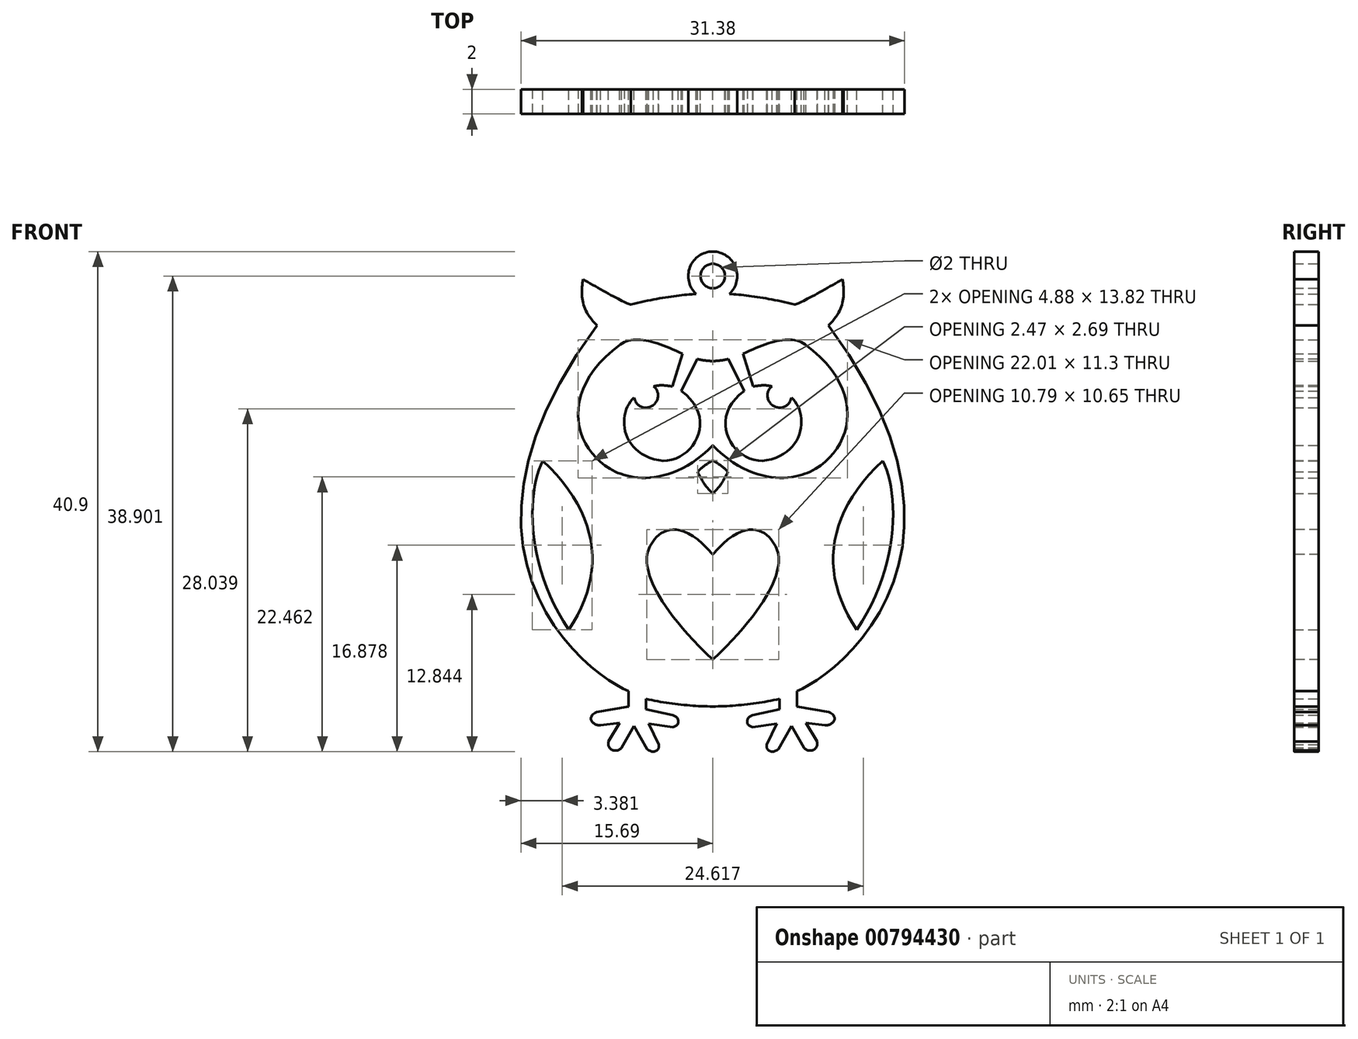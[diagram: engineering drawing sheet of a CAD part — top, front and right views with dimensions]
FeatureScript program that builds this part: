
annotation { "Feature Type Name" : "Feature", "Feature Type Description" : "" }
export const myFeature = defineFeature(function(context is Context, id is Id, definition is map)
    precondition{}
    {
        {
            var Q0;
            Q0=qCreatedBy(makeId("Front.planeOp"),FACE);
            var sketch = newSketch(context, id + "F0", { "sketchPlane" : qUnion([Q0])});
            skLineSegment(sketch, "E0", {"start": v(-16.23, -20) * mm, "end": v(16.23, 20) * mm, "construction": true});
            skFitSpline(sketch, "E1", {"points": [v(-6.7, 17.41) * mm, v(0, 18.33) * mm], "startDerivative": vector(8.77, 2.26) * mm, "endDerivative": vector(4.3, 0) * mm});
            skFitSpline(sketch, "E2", {"points": [v(-6.7, 17.41) * mm, v(-10.62, 19.48) * mm], "startDerivative": vector(-0.95, 0) * mm, "endDerivative": vector(-4.32, 2.45) * mm});
            skFitSpline(sketch, "E3", {"points": [v(-10.62, 19.48) * mm, v(-9.46, 15.72) * mm], "startDerivative": vector(-0.45, -3.6) * mm, "endDerivative": vector(4.32, -4) * mm});
            skFitSpline(sketch, "E4", {"points": [v(-9.46, 15.72) * mm, v(-6.88, -14.19) * mm], "startDerivative": vector(-42.09, -56.82) * mm, "endDerivative": vector(8.88, -3.32) * mm});
            skFitSpline(sketch, "E5", {"points": [v(-6.88, -14.19) * mm, v(-6.88, -15.47) * mm], "startDerivative": vector(0, -1.28) * mm, "endDerivative": vector(0, -1.28) * mm});
            skFitSpline(sketch, "E6", {"points": [v(-6.88, -15.47) * mm, v(-9.5, -15.9) * mm], "startDerivative": vector(-2.62, -0.44) * mm, "endDerivative": vector(-2.62, -0.44) * mm});
            skFitSpline(sketch, "E7", {"points": [v(-9.5, -15.9) * mm, v(-9.18, -16.99) * mm], "startDerivative": vector(-2.96, -1.5) * mm, "endDerivative": vector(1.5, 0.32) * mm});
            skFitSpline(sketch, "E8", {"points": [v(-9.18, -16.99) * mm, v(-7.63, -16.8) * mm], "startDerivative": vector(1.55, 0.18) * mm, "endDerivative": vector(1.55, 0.18) * mm});
            skFitSpline(sketch, "E9", {"points": [v(-7.63, -16.8) * mm, v(-8.53, -18.34) * mm], "startDerivative": vector(-0.9, -1.53) * mm, "endDerivative": vector(-0.9, -1.53) * mm});
            skFitSpline(sketch, "E10", {"points": [v(-8.53, -18.34) * mm, v(-7.47, -18.84) * mm], "startDerivative": vector(-0.36, -2.55) * mm, "endDerivative": vector(0.87, 1.14) * mm});
            skFitSpline(sketch, "E11", {"points": [v(-7.47, -18.84) * mm, v(-6.45, -17.05) * mm], "startDerivative": vector(1.02, 1.8) * mm, "endDerivative": vector(1.02, 1.8) * mm});
            skFitSpline(sketch, "E12", {"points": [v(-6.45, -17.05) * mm, v(-5.37, -18.98) * mm], "startDerivative": vector(1.08, -1.93) * mm, "endDerivative": vector(1.08, -1.93) * mm});
            skFitSpline(sketch, "E13", {"points": [v(-5.37, -18.98) * mm, v(-4.43, -18.58) * mm], "startDerivative": vector(2.05, -1.28) * mm, "endDerivative": vector(-0.32, 1.1) * mm});
            skFitSpline(sketch, "E14", {"points": [v(-4.43, -18.58) * mm, v(-5.23, -16.88) * mm], "startDerivative": vector(-0.8, 1.7) * mm, "endDerivative": vector(-0.8, 1.7) * mm});
            skFitSpline(sketch, "E15", {"points": [v(-5.23, -16.88) * mm, v(-3.26, -17.14) * mm], "startDerivative": vector(1.97, -0.26) * mm, "endDerivative": vector(1.97, -0.26) * mm});
            skFitSpline(sketch, "E16", {"points": [v(-3.26, -17.14) * mm, v(-3.26, -16.18) * mm], "startDerivative": vector(1.96, 0.27) * mm, "endDerivative": vector(-1.6, 0.32) * mm});
            skFitSpline(sketch, "E17", {"points": [v(-3.26, -16.18) * mm, v(-5.46, -15.68) * mm], "startDerivative": vector(-2.2, 0.5) * mm, "endDerivative": vector(-2.2, 0.5) * mm});
            skFitSpline(sketch, "E18", {"points": [v(-5.46, -15.68) * mm, v(-5.46, -14.83) * mm], "startDerivative": vector(0, 0.85) * mm, "endDerivative": vector(0, 0.85) * mm});
            skFitSpline(sketch, "E19", {"points": [v(-5.46, -14.83) * mm, v(0, -15.47) * mm], "startDerivative": vector(5.42, -1.32) * mm, "endDerivative": vector(5.24, -0.12) * mm});
            skFitSpline(sketch, "E20", {"points": [v(-13.9, 4.64) * mm, v(-11.77, -9.18) * mm], "startDerivative": vector(-4.05, -7.66) * mm, "endDerivative": vector(10.64, -15.64) * mm});
            skFitSpline(sketch, "E21", {"points": [v(-13.9, 4.64) * mm, v(-11.77, -9.18) * mm], "startDerivative": vector(13.96, -13.18) * mm, "endDerivative": vector(-9.2, -13.72) * mm});
            skFitSpline(sketch, "E22", {"points": [v(0, 12.8) * mm, v(-1.27, 12.97) * mm], "startDerivative": vector(-1.5, 0.04) * mm, "endDerivative": vector(-1.22, 0.31) * mm});
            skFitSpline(sketch, "E23", {"points": [v(-1.27, 12.97) * mm, v(-2.57, 10.35) * mm], "startDerivative": vector(-1.3, -2.62) * mm, "endDerivative": vector(-1.3, -2.62) * mm});
            skFitSpline(sketch, "E24", {"points": [v(-2.57, 10.35) * mm, v(-4.8, 4.76) * mm], "startDerivative": vector(9.95, -7.21) * mm, "endDerivative": vector(-8.57, 2.6) * mm});
            skFitSpline(sketch, "E25", {"points": [v(-4.8, 4.76) * mm, v(-6.43, 9.81) * mm], "startDerivative": vector(-8.74, 2.65) * mm, "endDerivative": vector(3.84, 3.47) * mm});
            skFitSpline(sketch, "E26", {"points": [v(-6.43, 9.81) * mm, v(-4.84, 9.21) * mm], "startDerivative": vector(0.77, -3.16) * mm, "endDerivative": vector(1.08, 0.94) * mm});
            skFitSpline(sketch, "E27", {"points": [v(-4.84, 9.21) * mm, v(-4.84, 10.71) * mm], "startDerivative": vector(1.62, 1.4) * mm, "endDerivative": vector(-1.29, 0.77) * mm});
            skFitSpline(sketch, "E28", {"points": [v(-4.84, 10.71) * mm, v(-3.32, 10.71) * mm], "startDerivative": vector(1.16, 0.39) * mm, "endDerivative": vector(2, -0.39) * mm});
            skFitSpline(sketch, "E29", {"points": [v(-3.32, 10.71) * mm, v(-2.48, 13.38) * mm], "startDerivative": vector(0.84, 2.66) * mm, "endDerivative": vector(0.84, 2.66) * mm});
            skFitSpline(sketch, "E30", {"points": [v(-2.48, 13.38) * mm, v(-7.55, 14.15) * mm], "startDerivative": vector(-6.19, 3.03) * mm, "endDerivative": vector(-3.45, -2.5) * mm});
            skFitSpline(sketch, "E31", {"points": [v(-7.55, 14.15) * mm, v(-7.98, 3.75) * mm], "startDerivative": vector(-15.56, -11.26) * mm, "endDerivative": vector(10.36, -5) * mm});
            skFitSpline(sketch, "E32", {"points": [v(-7.98, 3.75) * mm, v(0, 5.9) * mm], "startDerivative": vector(4.78, -2.3) * mm, "endDerivative": vector(9.63, 9.73) * mm});
            skFitSpline(sketch, "E33", {"points": [v(0, 4.66) * mm, v(-1.23, 3.73) * mm], "startDerivative": vector(-1.31, -0.7) * mm, "endDerivative": vector(-1.03, -1.22) * mm});
            skFitSpline(sketch, "E34", {"points": [v(-1.23, 3.73) * mm, v(0, 1.97) * mm], "startDerivative": vector(0.97, -1.93) * mm, "endDerivative": vector(1.83, -1.55) * mm});
            skLineSegment(sketch, "E35", {"start": v(0, 18.33) * mm, "end": v(0, -15.47) * mm, "construction": true});
            skFitSpline(sketch, "E36.MirrorCS", {"points": [v(3.26, -17.14) * mm, v(3.26, -16.18) * mm], "startDerivative": vector(-1.96, 0.27) * mm, "endDerivative": vector(1.6, 0.32) * mm});
            skFitSpline(sketch, "E37.MirrorCS", {"points": [v(6.88, -14.19) * mm, v(6.88, -15.47) * mm], "startDerivative": vector(0, -1.28) * mm, "endDerivative": vector(0, -1.28) * mm});
            skFitSpline(sketch, "E38.MirrorCS", {"points": [v(7.63, -16.8) * mm, v(8.53, -18.34) * mm], "startDerivative": vector(0.9, -1.53) * mm, "endDerivative": vector(0.9, -1.53) * mm});
            skFitSpline(sketch, "E39.MirrorCS", {"points": [v(9.18, -16.99) * mm, v(7.63, -16.8) * mm], "startDerivative": vector(-1.55, 0.18) * mm, "endDerivative": vector(-1.55, 0.18) * mm});
            skFitSpline(sketch, "E40.MirrorCS", {"points": [v(0, 4.66) * mm, v(1.23, 3.73) * mm], "startDerivative": vector(1.31, -0.7) * mm, "endDerivative": vector(1.03, -1.22) * mm});
            skFitSpline(sketch, "E41.MirrorCS", {"points": [v(4.84, 10.71) * mm, v(3.32, 10.71) * mm], "startDerivative": vector(-1.16, 0.39) * mm, "endDerivative": vector(-2, -0.39) * mm});
            skFitSpline(sketch, "E42.MirrorCS", {"points": [v(4.84, 9.21) * mm, v(4.84, 10.71) * mm], "startDerivative": vector(-1.62, 1.4) * mm, "endDerivative": vector(1.29, 0.77) * mm});
            skFitSpline(sketch, "E43.MirrorCS", {"points": [v(5.46, -15.68) * mm, v(5.46, -14.83) * mm], "startDerivative": vector(0, 0.85) * mm, "endDerivative": vector(0, 0.85) * mm});
            skFitSpline(sketch, "E44.MirrorCS", {"points": [v(0, 12.8) * mm, v(1.27, 12.97) * mm], "startDerivative": vector(1.5, 0.04) * mm, "endDerivative": vector(1.22, 0.31) * mm});
            skFitSpline(sketch, "E45.MirrorCS", {"points": [v(5.37, -18.98) * mm, v(4.43, -18.58) * mm], "startDerivative": vector(-2.05, -1.28) * mm, "endDerivative": vector(0.32, 1.1) * mm});
            skFitSpline(sketch, "E46.MirrorCS", {"points": [v(8.53, -18.34) * mm, v(7.47, -18.84) * mm], "startDerivative": vector(0.36, -2.55) * mm, "endDerivative": vector(-0.87, 1.14) * mm});
            skFitSpline(sketch, "E47.MirrorCS", {"points": [v(7.47, -18.84) * mm, v(6.45, -17.05) * mm], "startDerivative": vector(-1.02, 1.8) * mm, "endDerivative": vector(-1.02, 1.8) * mm});
            skFitSpline(sketch, "E48.MirrorCS", {"points": [v(3.26, -16.18) * mm, v(5.46, -15.68) * mm], "startDerivative": vector(2.2, 0.5) * mm, "endDerivative": vector(2.2, 0.5) * mm});
            skFitSpline(sketch, "E49.MirrorCS", {"points": [v(6.45, -17.05) * mm, v(5.37, -18.98) * mm], "startDerivative": vector(-1.08, -1.93) * mm, "endDerivative": vector(-1.08, -1.93) * mm});
            skFitSpline(sketch, "E50.MirrorCS", {"points": [v(5.23, -16.88) * mm, v(3.26, -17.14) * mm], "startDerivative": vector(-1.97, -0.26) * mm, "endDerivative": vector(-1.97, -0.26) * mm});
            skFitSpline(sketch, "E51.MirrorCS", {"points": [v(4.43, -18.58) * mm, v(5.23, -16.88) * mm], "startDerivative": vector(0.8, 1.7) * mm, "endDerivative": vector(0.8, 1.7) * mm});
            skFitSpline(sketch, "E52.MirrorCS", {"points": [v(1.27, 12.97) * mm, v(2.57, 10.35) * mm], "startDerivative": vector(1.3, -2.62) * mm, "endDerivative": vector(1.3, -2.62) * mm});
            skFitSpline(sketch, "E53.MirrorCS", {"points": [v(6.7, 17.41) * mm, v(10.62, 19.48) * mm], "startDerivative": vector(0.95, 0) * mm, "endDerivative": vector(4.32, 2.45) * mm});
            skFitSpline(sketch, "E54.MirrorCS", {"points": [v(10.62, 19.48) * mm, v(9.46, 15.72) * mm], "startDerivative": vector(0.45, -3.6) * mm, "endDerivative": vector(-4.32, -4) * mm});
            skFitSpline(sketch, "E55.MirrorCS", {"points": [v(6.88, -15.47) * mm, v(9.5, -15.9) * mm], "startDerivative": vector(2.62, -0.44) * mm, "endDerivative": vector(2.62, -0.44) * mm});
            skFitSpline(sketch, "E56.MirrorCS", {"points": [v(9.5, -15.9) * mm, v(9.18, -16.99) * mm], "startDerivative": vector(2.96, -1.5) * mm, "endDerivative": vector(-1.5, 0.32) * mm});
            skFitSpline(sketch, "E57.MirrorCS", {"points": [v(1.23, 3.73) * mm, v(0, 1.97) * mm], "startDerivative": vector(-0.97, -1.93) * mm, "endDerivative": vector(-1.83, -1.55) * mm});
            skFitSpline(sketch, "E58.MirrorCS", {"points": [v(6.43, 9.81) * mm, v(4.84, 9.21) * mm], "startDerivative": vector(-0.77, -3.16) * mm, "endDerivative": vector(-1.08, 0.94) * mm});
            skFitSpline(sketch, "E59.MirrorCS", {"points": [v(3.32, 10.71) * mm, v(2.48, 13.38) * mm], "startDerivative": vector(-0.84, 2.66) * mm, "endDerivative": vector(-0.84, 2.66) * mm});
            skFitSpline(sketch, "E60.MirrorCS", {"points": [v(2.48, 13.38) * mm, v(7.55, 14.15) * mm], "startDerivative": vector(6.19, 3.03) * mm, "endDerivative": vector(3.45, -2.5) * mm});
            skLineSegment(sketch, "E61.MirrorCS", {"start": v(16.23, -20) * mm, "end": v(-16.23, 20) * mm, "construction": true});
            skFitSpline(sketch, "E62.MirrorCS", {"points": [v(6.7, 17.41) * mm, v(0, 18.33) * mm], "startDerivative": vector(-8.77, 2.26) * mm, "endDerivative": vector(-4.3, 0) * mm});
            skFitSpline(sketch, "E63.MirrorCS", {"points": [v(2.57, 10.35) * mm, v(4.8, 4.76) * mm], "startDerivative": vector(-9.95, -7.21) * mm, "endDerivative": vector(8.57, 2.6) * mm});
            skFitSpline(sketch, "E64.MirrorCS", {"points": [v(9.46, 15.72) * mm, v(6.88, -14.19) * mm], "startDerivative": vector(42.09, -56.82) * mm, "endDerivative": vector(-8.88, -3.32) * mm});
            skFitSpline(sketch, "E65.MirrorCS", {"points": [v(4.8, 4.76) * mm, v(6.43, 9.81) * mm], "startDerivative": vector(8.74, 2.65) * mm, "endDerivative": vector(-3.84, 3.47) * mm});
            skFitSpline(sketch, "E66.MirrorCS", {"points": [v(7.98, 3.75) * mm, v(0, 5.9) * mm], "startDerivative": vector(-4.78, -2.3) * mm, "endDerivative": vector(-9.63, 9.73) * mm});
            skFitSpline(sketch, "E67.MirrorCS", {"points": [v(5.46, -14.83) * mm, v(0, -15.47) * mm], "startDerivative": vector(-5.42, -1.32) * mm, "endDerivative": vector(-5.24, -0.12) * mm});
            skFitSpline(sketch, "E68.MirrorCS", {"points": [v(13.9, 4.64) * mm, v(11.77, -9.18) * mm], "startDerivative": vector(4.05, -7.66) * mm, "endDerivative": vector(-10.64, -15.64) * mm});
            skFitSpline(sketch, "E69.MirrorCS", {"points": [v(7.55, 14.15) * mm, v(7.98, 3.75) * mm], "startDerivative": vector(15.56, -11.26) * mm, "endDerivative": vector(-10.36, -5) * mm});
            skFitSpline(sketch, "E70.MirrorCS", {"points": [v(13.9, 4.64) * mm, v(11.77, -9.18) * mm], "startDerivative": vector(-13.96, -13.18) * mm, "endDerivative": vector(9.2, -13.72) * mm});
            skCircle(sketch, "E71", {"center": v(0, 19.75) * mm, "radius": 2 * mm});
            skCircle(sketch, "E72", {"center": v(0, 19.75) * mm, "radius": 1 * mm});
            skPoint(sketch, "E73", {"position": v(0, 20) * mm});
            skSolve(sketch);
        }
        {
            var Q0;
            Q0 = qSketchRegion(id + "F0", true);
            extrude(context, id + "F1", {"entities" : qUnion([Q0]), "depth" : 2 * mm, "offsetDistance" : 25 * mm});
        }
        {
            var Q0;
            Q0=makeQuery(id+"F1.opExtrude","CAP_FACE",FACE,{"disambiguationData":[OSD([sQuery(id+"F0.wireOp",EDGE,"E1"),sQuery(id+"F0.wireOp",EDGE,"E2"),sQuery(id+"F0.wireOp",EDGE,"E3"),sQuery(id+"F0.wireOp",EDGE,"E4"),sQuery(id+"F0.wireOp",EDGE,"E5"),sQuery(id+"F0.wireOp",EDGE,"E6"),sQuery(id+"F0.wireOp",EDGE,"E7"),sQuery(id+"F0.wireOp",EDGE,"E8"),sQuery(id+"F0.wireOp",EDGE,"E9"),sQuery(id+"F0.wireOp",EDGE,"E10"),sQuery(id+"F0.wireOp",EDGE,"E11"),sQuery(id+"F0.wireOp",EDGE,"E12"),sQuery(id+"F0.wireOp",EDGE,"E13"),sQuery(id+"F0.wireOp",EDGE,"E14"),sQuery(id+"F0.wireOp",EDGE,"E15"),sQuery(id+"F0.wireOp",EDGE,"E16"),sQuery(id+"F0.wireOp",EDGE,"E17"),sQuery(id+"F0.wireOp",EDGE,"E18"),sQuery(id+"F0.wireOp",EDGE,"E19"),sQuery(id+"F0.wireOp",EDGE,"E20"),sQuery(id+"F0.wireOp",EDGE,"E21"),sQuery(id+"F0.wireOp",EDGE,"E22"),sQuery(id+"F0.wireOp",EDGE,"E23"),sQuery(id+"F0.wireOp",EDGE,"E24"),sQuery(id+"F0.wireOp",EDGE,"E25"),sQuery(id+"F0.wireOp",EDGE,"E26"),sQuery(id+"F0.wireOp",EDGE,"E27"),sQuery(id+"F0.wireOp",EDGE,"E28"),sQuery(id+"F0.wireOp",EDGE,"E29"),sQuery(id+"F0.wireOp",EDGE,"E30"),sQuery(id+"F0.wireOp",EDGE,"E31"),sQuery(id+"F0.wireOp",EDGE,"E32"),sQuery(id+"F0.wireOp",EDGE,"E33"),sQuery(id+"F0.wireOp",EDGE,"E34"),sQuery(id+"F0.wireOp",EDGE,"E36.MirrorCS"),sQuery(id+"F0.wireOp",EDGE,"E37.MirrorCS"),sQuery(id+"F0.wireOp",EDGE,"E38.MirrorCS"),sQuery(id+"F0.wireOp",EDGE,"E39.MirrorCS"),sQuery(id+"F0.wireOp",EDGE,"E40.MirrorCS"),sQuery(id+"F0.wireOp",EDGE,"E41.MirrorCS"),sQuery(id+"F0.wireOp",EDGE,"E42.MirrorCS"),sQuery(id+"F0.wireOp",EDGE,"E43.MirrorCS"),sQuery(id+"F0.wireOp",EDGE,"E44.MirrorCS"),sQuery(id+"F0.wireOp",EDGE,"E45.MirrorCS"),sQuery(id+"F0.wireOp",EDGE,"E46.MirrorCS"),sQuery(id+"F0.wireOp",EDGE,"E47.MirrorCS"),sQuery(id+"F0.wireOp",EDGE,"E48.MirrorCS"),sQuery(id+"F0.wireOp",EDGE,"E49.MirrorCS"),sQuery(id+"F0.wireOp",EDGE,"E50.MirrorCS"),sQuery(id+"F0.wireOp",EDGE,"E51.MirrorCS"),sQuery(id+"F0.wireOp",EDGE,"E52.MirrorCS"),sQuery(id+"F0.wireOp",EDGE,"E53.MirrorCS"),sQuery(id+"F0.wireOp",EDGE,"E54.MirrorCS"),sQuery(id+"F0.wireOp",EDGE,"E55.MirrorCS"),sQuery(id+"F0.wireOp",EDGE,"E56.MirrorCS"),sQuery(id+"F0.wireOp",EDGE,"E57.MirrorCS"),sQuery(id+"F0.wireOp",EDGE,"E58.MirrorCS"),sQuery(id+"F0.wireOp",EDGE,"E59.MirrorCS"),sQuery(id+"F0.wireOp",EDGE,"E60.MirrorCS"),sQuery(id+"F0.wireOp",EDGE,"E62.MirrorCS"),sQuery(id+"F0.wireOp",EDGE,"E63.MirrorCS"),sQuery(id+"F0.wireOp",EDGE,"E64.MirrorCS"),sQuery(id+"F0.wireOp",EDGE,"E65.MirrorCS"),sQuery(id+"F0.wireOp",EDGE,"E66.MirrorCS"),sQuery(id+"F0.wireOp",EDGE,"E67.MirrorCS"),sQuery(id+"F0.wireOp",EDGE,"E68.MirrorCS"),sQuery(id+"F0.wireOp",EDGE,"E69.MirrorCS"),sQuery(id+"F0.wireOp",EDGE,"E70.MirrorCS"),sQuery(id+"F0.wireOp",EDGE,"E71"),sQuery(id+"F0.wireOp",EDGE,"E72")])],"isStart":false});
            var sketch = newSketch(context, id + "F2", { "sketchPlane" : qUnion([Q0])});
            skLineSegment(sketch, "E74", {"start": v(0, 0) * mm, "end": v(0, -15.47) * mm, "construction": true});
            skFitSpline(sketch, "E75", {"points": [v(0, -11.63) * mm, v(-5.37, -3.03) * mm], "startDerivative": vector(-13.5, 12.8) * mm, "endDerivative": vector(0.76, 4.57) * mm});
            skFitSpline(sketch, "E76", {"points": [v(-5.37, -3.03) * mm, v(0, -3.03) * mm], "startDerivative": vector(0.54, 3.25) * mm, "endDerivative": vector(10.25, -12.03) * mm});
            skFitSpline(sketch, "E77.MirrorCS", {"points": [v(5.37, -3.03) * mm, v(0, -3.03) * mm], "startDerivative": vector(-0.54, 3.25) * mm, "endDerivative": vector(-10.25, -12.03) * mm});
            skFitSpline(sketch, "E78.MirrorCS", {"points": [v(0, -11.63) * mm, v(5.37, -3.03) * mm], "startDerivative": vector(13.5, 12.8) * mm, "endDerivative": vector(-0.76, 4.57) * mm});
            skSolve(sketch);
        }
        {
            var Q0;
            Q0 = qSketchRegion(id + "F2", true);
            extrude(context, id + "F3", {"entities" : qUnion([Q0]), "operationType" : NewBodyOperationType.REMOVE, "endBound" : BoundingType.THROUGH_ALL, "oppositeDirection" : true, "depth" : 25 * mm, "offsetDistance" : 25 * mm});
        }
    });
